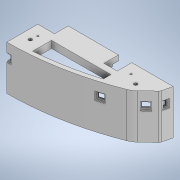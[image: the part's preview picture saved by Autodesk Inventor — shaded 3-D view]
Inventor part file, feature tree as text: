
AUTODESK INVENTOR PART (.ipt)
format: ipt  version: 2020 (Build 240168000, 168)  size: 527,360 bytes
history: native  units: mm
features: sketch x14, extrude x13, projected_geometry x7, other x6, hole x2, fillet x2
ambient origin geometry x8: Origin, YZ Plane, XZ Plane, XY Plane, X Axis, Y Axis, Z Axis, Center Point
bodies: Body1 (feature_tree)
feature tree (44):
  sketch  "스케치1"
  extrude  "돌출11"  Depth=657.5mm
  other  "작업 평면1"
  extrude  "돌출13"  Depth=585.0mm
  other  "작업 평면2"
  extrude  "돌출14"  Depth=0.872665mm
  other  "작업 평면3"
  extrude  "돌출15"  Depth=1299.898854mm
  other  "작업 평면4"
  extrude  "돌출16"  Depth=2.356194mm
  extrude  "돌출17"  Depth=999.812583mm
  extrude  "돌출18"  Depth=2.094395mm
  hole  "구멍3"  [1 undecoded]
  extrude  "돌출19"  Depth=1.745329mm
  hole  "구멍4"  [1 undecoded]
  extrude  "돌출20"  Depth=2.356194mm
  extrude  "돌출21"  Depth=2.356194mm
  other  "작업 평면5"
  extrude  "돌출22"  Depth=2.356194mm
  other  "작업 평면6"
  extrude  "돌출23"  Depth=2.356194mm
  fillet  "모깎기1"  Radius=2.356194mm
  fillet  "모깎기2"  Radius=2.356194mm
  extrude  "돌출24"  Depth=1.745329mm
  sketch  "스케치14"
  sketch  "스케치15"
  sketch  "스케치16"
  sketch  "스케치17"
  sketch  "스케치18"
  sketch  "스케치19"
  projected_geometry  "투영된 루프14"
  sketch  "스케치20"
  projected_geometry  "투영된 루프16"
  sketch  "스케치21"
  projected_geometry  "투영된 루프17"
  projected_geometry  "투영된 루프18"
  projected_geometry  "투영된 루프21"
  sketch  "스케치22"
  sketch  "스케치23"
  sketch  "스케치24"
  sketch  "스케치25"
  projected_geometry  "투영된 루프22"
  sketch  "스케치26"
  projected_geometry  "투영된 루프23"
note: 2 required parameter values undecoded (feature->parameter linkage not recoverable at this tier; creation-order binding heuristic only, values carry confidence <= 0.55)
